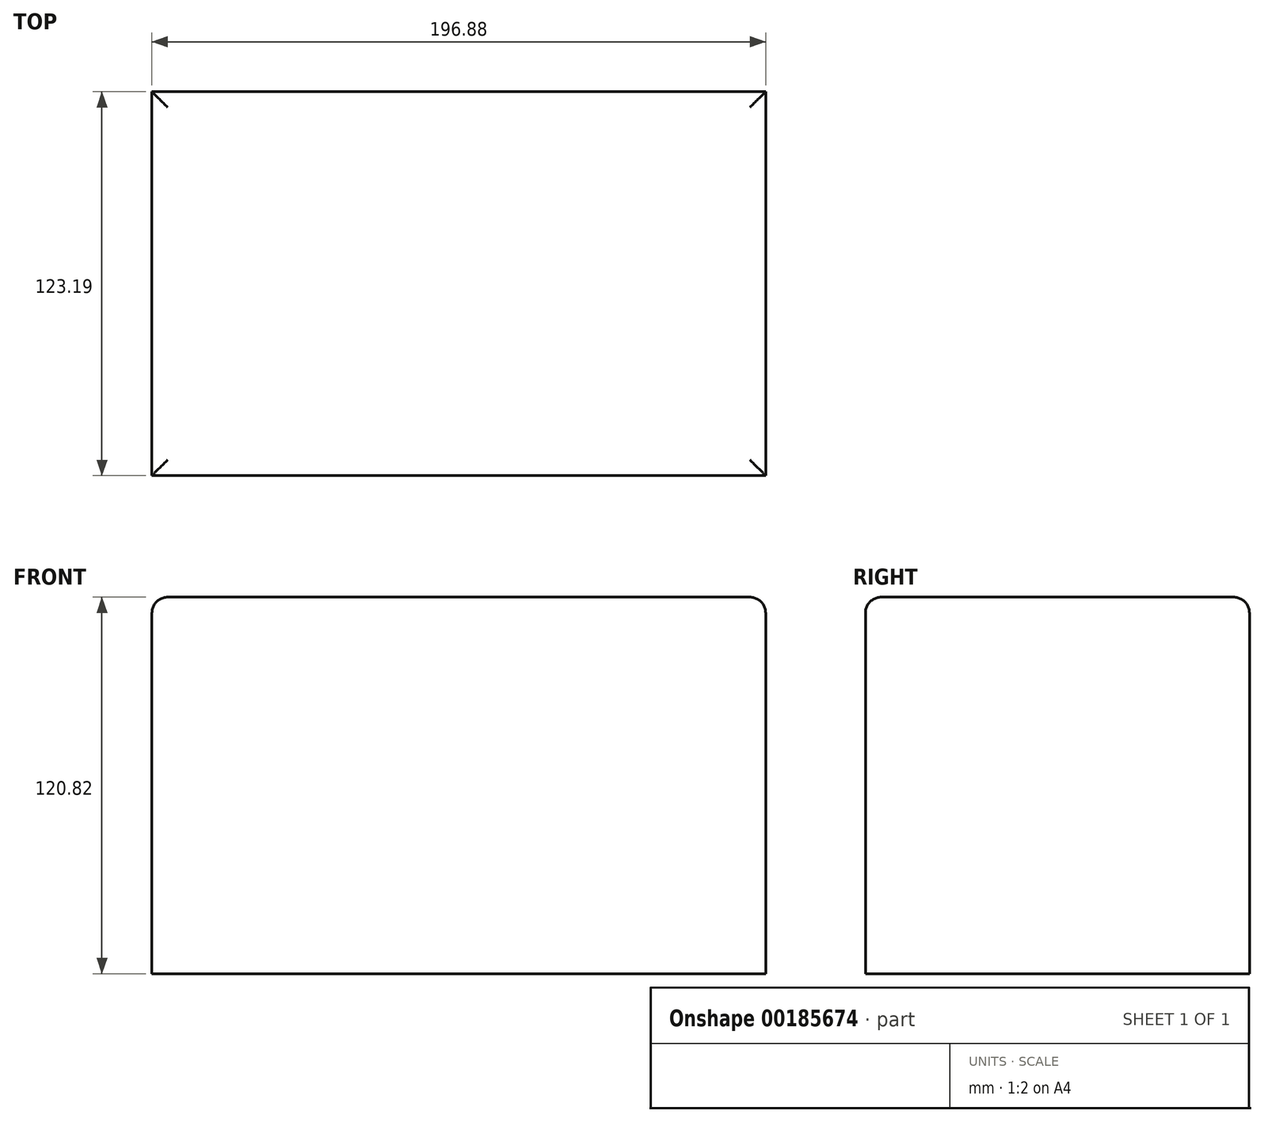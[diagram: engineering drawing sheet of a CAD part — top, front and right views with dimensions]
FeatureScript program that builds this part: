
annotation { "Feature Type Name" : "Feature", "Feature Type Description" : "" }
export const myFeature = defineFeature(function(context is Context, id is Id, definition is map)
    precondition{}
    {
        {
            var Q0;
            Q0=qCreatedBy(makeId("Front.planeOp"),FACE);
            var sketch = newSketch(context, id + "F0", { "sketchPlane" : qUnion([Q0])});
            skLineSegment(sketch, "E0.bottom", {"start": v(-138.18, 66.34) * mm, "end": v(58.7, 66.34) * mm});
            skLineSegment(sketch, "E0.top", {"start": v(-138.18, -54.48) * mm, "end": v(58.7, -54.48) * mm});
            skLineSegment(sketch, "E0.left", {"start": v(-138.18, 66.34) * mm, "end": v(-138.18, -54.48) * mm});
            skLineSegment(sketch, "E0.right", {"start": v(58.7, 66.34) * mm, "end": v(58.7, -54.48) * mm});
            skSolve(sketch);
        }
        {
            var Q0;
            Q0 = qSketchRegion(id + "F0", true);
            extrude(context, id + "F1", {"entities" : qUnion([Q0]), "oppositeDirection" : true, "depth" : 123.19 * mm});
        }
        {
            var Q0;
            Q0=makeQuery(id+"F1.opExtrude","SWEPT_FACE",FACE,{"disambiguationData":[OSD([sQuery(id+"F0.wireOp",EDGE,"E0.bottom")])]});
            fillet(context, id + "F2", {"entities" : qUnion([Q0]), "radius" : 5.08 * mm, "tangentPropagation" : true, "allowEdgeOverflow" : false});
        }
    });
